# Revit family: KS, ALU-PU 80, DS 20, M10-M12, Ø 42-168,3
name_source: partatom
category: HLS-Bauteile
revit_build: Autodesk Revit 2017 (Build: 20190507_1515(x64)
units: mm (PartAtom-declared; Revit-internal decimal feet)

## family parameters
Arbeitsebenenbasiert = Ja
Beim Laden mit Abzugskörper schneiden = Nein
Bemaßung runder Anschluss = Durchmesser verwenden
Gemeinsam genutzt = Ja
Immer vertikal = Nein
Raumberechnungspunkt = Nein
Teiletyp = Normal

## types (15) — shared parameters
Anschluss = M10/M12
Baustoffklasse = B2
DS = 20 mm  [stored 0.0656168 ft]
DVS = 18 mm  [stored 0.0590551 ft]
Dichte Kern = 80 kg/m³
Dichte Mantel = 2.700 kg/m³
Dicke Mantel = 0,08 mm
Dämmkörper = ALU/PU
Dämmstärke = 20 mm  [stored 0.0656168 ft]
Fabrikat = MEFA
Firma = MEFA Befestigungs- und Montagesysteme GmbH
HGA = 22 mm  [stored 0.0721785 ft]
Kurztext1 = Kälteschelle RG80 ALU/PU
L = 100 mm
Material = Stahl
Material Mantel = Alufolie
Materialname = S235
Mengeneinheit = St
Oberflaeche = galvanisch verzinkt
Rohrschellentyp = Maxima PSM
Schalenlänge = 100 mm
Vorgabe-Ansicht = 1219 mm
Wasserdampfdiffusionswiderstand = 18750 µ
Wärmeleitfähigkeit = 0.025 W/mK
max. Temperaturbeständigkeit = 120 °C
mittl. Nenndruckfestigkeit Kern = 0,5 N/mm²
stat. Belastung Kern = 0,1 N/mm²
vpe = 1 St

## per-type parameters (varying)
- Kälteschelle ALU-PU 80, DS 20, M10/M12, Ø 42,4: A=45 mm  [stored 0.147638 ft]; AB=2 mm  [stored 0.00656168 ft]; Anschlußhöhe=46 mm; Artikelnummer=7560426; B=150 mm; Breite=151 mm; D=42 mm; D0=82 mm; DF1=31 mm  [stored 0.101706 ft]; DF2=30 mm  [stored 0.0984252 ft]; Dmax=43 mm  [stored 0.141076 ft]; Dmin=40 mm  [stored 0.131234 ft]; EAN=4250928443427; Gewicht=0.42 kg; Gewicht pro Bauteil=0.42 kg; H=110 mm; Kurztext2=42,4 mm Iso 20 x 100 mm M10/M12; MB=30 mm  [stored 0.0984252 ft]; MD=3 mm  [stored 0.00984252 ft]; R=41 mm; RM=44 mm; Rohraußendurchmesser Kupfer=42 mm; Rohraußendurchmesser Stahl=42,4 mm; S=119 mm; max. zul. Last=0.40 kN
- Kälteschelle ALU-PU 80, DS 20, M10/M12, Ø 48,3: A=45 mm  [stored 0.147638 ft]; AB=1 mm  [stored 0.00328084 ft]; Anschlußhöhe=44 mm; Artikelnummer=7560486; B=150 mm; Breite=151 mm; D=48 mm; D0=88 mm; DF1=27 mm  [stored 0.0885827 ft]; DF2=27 mm  [stored 0.0885827 ft]; Dmax=50 mm  [stored 0.164042 ft]; Dmin=47 mm  [stored 0.154199 ft]; EAN=4250928443441; Gewicht=0.42 kg; Gewicht pro Bauteil=0.42 kg; H=116 mm; Kurztext2=48,3 mm Iso 20 x 100 mm M10/M12; MB=30 mm  [stored 0.0984252 ft]; MD=3 mm  [stored 0.00984252 ft]; R=44 mm; RM=47 mm  [stored 0.154199 ft]; Rohraußendurchmesser Stahl=48,3 mm; S=123 mm; max. zul. Last=0.40 kN
- Kälteschelle ALU-PU 80, DS 20, M10/M12, Ø 54: A=45 mm  [stored 0.147638 ft]; AB=2 mm  [stored 0.00656168 ft]; Anschlußhöhe=46 mm; Artikelnummer=75605432; B=162 mm; Breite=162 mm; D=54 mm  [stored 0.177165 ft]; D0=94 mm; DF1=29 mm  [stored 0.0951444 ft]; DF2=29 mm  [stored 0.0951444 ft]; Dmax=58 mm  [stored 0.190289 ft]; Dmin=52 mm; EAN=4250928443472; Gewicht=0.46 kg; Gewicht pro Bauteil=0.46 kg; H=122 mm; Kurztext2=54 mm Iso 20 x 100 mm M10/M12; MB=30 mm  [stored 0.0984252 ft]; MD=3 mm  [stored 0.00984252 ft]; R=47 mm  [stored 0.154199 ft]; RM=50 mm  [stored 0.164042 ft]; Rohraußendurchmesser Kupfer=54 mm; S=133 mm; max. zul. Last=0.40 kN
- Kälteschelle ALU-PU 80, DS 20, M10/M12, Ø 57: A=45 mm  [stored 0.147638 ft]; AB=1 mm  [stored 0.00328084 ft]; Anschlußhöhe=45 mm; Artikelnummer=75605742; B=162 mm; Breite=162 mm; D=57 mm  [stored 0.187008 ft]; D0=97 mm; DF1=28 mm  [stored 0.0918635 ft]; DF2=28 mm  [stored 0.0918635 ft]; Dmax=60 mm  [stored 0.19685 ft]; Dmin=56 mm  [stored 0.183727 ft]; EAN=4250928443489; Gewicht=0.46 kg; Gewicht pro Bauteil=0.46 kg; H=125 mm; Kurztext2=57 mm Iso 20 x 100 mm M10/M12; MB=30 mm  [stored 0.0984252 ft]; MD=3 mm  [stored 0.00984252 ft]; R=49 mm; RM=52 mm; Rohraußendurchmesser Stahl=57 mm; S=134 mm; max. zul. Last=0.40 kN
- Kälteschelle ALU-PU 80, DS 20, M10/M12, Ø 60,3: A=45 mm  [stored 0.147638 ft]; AB=2 mm  [stored 0.00656168 ft]; Anschlußhöhe=44 mm; Artikelnummer=7560606; B=162 mm; Breite=162 mm; D=60 mm  [stored 0.19685 ft]; D0=100 mm; DF1=27 mm  [stored 0.0885827 ft]; DF2=27 mm  [stored 0.0885827 ft]; Dmax=62 mm  [stored 0.203412 ft]; Dmin=58 mm  [stored 0.190289 ft]; EAN=4250928443502; Gewicht=0.46 kg; Gewicht pro Bauteil=0.46 kg; H=128 mm; Kurztext2=60,3 mm Iso 20 x 100 mm M10/M12; MB=30 mm  [stored 0.0984252 ft]; MD=3 mm  [stored 0.00984252 ft]; R=50 mm  [stored 0.164042 ft]; RM=53 mm; Rohraußendurchmesser Stahl=60,3 mm; S=135 mm; max. zul. Last=0.40 kN
- Kälteschelle ALU-PU 80, DS 20, M10/M12, Ø 63,5: A=45 mm  [stored 0.147638 ft]; AB=2 mm  [stored 0.00656168 ft]; Anschlußhöhe=46 mm; Artikelnummer=75606442; B=172 mm; Breite=172 mm; D=64 mm; D0=104 mm; DF1=30 mm  [stored 0.0984252 ft]; DF2=30 mm  [stored 0.0984252 ft]; Dmax=66 mm  [stored 0.216535 ft]; Dmin=62 mm  [stored 0.203412 ft]; EAN=4250928443526; Gewicht=0.49 kg; Gewicht pro Bauteil=0.49 kg; H=132 mm; Kurztext2=63,5 mm Iso 20 x 100 mm M10/M12; MB=30 mm  [stored 0.0984252 ft]; MD=3 mm  [stored 0.00984252 ft]; R=52 mm; RM=55 mm  [stored 0.180446 ft]; Rohraußendurchmesser Stahl=63,5 mm; S=142 mm; max. zul. Last=0.50 kN
- Kälteschelle ALU-PU 80, DS 20, M10/M12, Ø 70: A=45 mm  [stored 0.147638 ft]; AB=2 mm  [stored 0.00656168 ft]; Anschlußhöhe=44 mm; Artikelnummer=75607042; B=172 mm; Breite=172 mm; D=70 mm; D0=110 mm; DF1=27 mm  [stored 0.0885827 ft]; DF2=27 mm  [stored 0.0885827 ft]; Dmax=72 mm; Dmin=68 mm; EAN=4250928443540; Gewicht=0.48 kg; Gewicht pro Bauteil=0.48 kg; H=138 mm; Kurztext2=70 mm Iso 20 x 100 mm M10/M12; MB=30 mm  [stored 0.0984252 ft]; MD=3 mm  [stored 0.00984252 ft]; R=55 mm  [stored 0.180446 ft]; RM=58 mm  [stored 0.190289 ft]; Rohraußendurchmesser Stahl=70 mm; S=145 mm; max. zul. Last=0.50 kN
- Kälteschelle ALU-PU 80, DS 20, M10/M12, Ø 76,1: A=45 mm  [stored 0.147638 ft]; AB=2 mm  [stored 0.00656168 ft]; Anschlußhöhe=47 mm; Artikelnummer=7560766; B=184 mm; Breite=184 mm; D=76 mm; D0=116 mm; DF1=29 mm  [stored 0.0951444 ft]; DF2=29 mm  [stored 0.0951444 ft]; Dmax=80 mm; Dmin=74 mm; EAN=4250928443571; Gewicht=0.53 kg; Gewicht pro Bauteil=0.53 kg; H=144 mm; Kurztext2=76,1 mm Iso 20 x 100 mm M10/M12; MB=30 mm  [stored 0.0984252 ft]; MD=3 mm  [stored 0.00984252 ft]; R=58 mm  [stored 0.190289 ft]; RM=61 mm; Rohraußendurchmesser Stahl=76,1 mm; S=155 mm; max. zul. Last=0.50 kN
- Kälteschelle ALU-PU 80, DS 20, M10/M12, Ø 88,9: A=46 mm  [stored 0.150919 ft]; AB=3 mm  [stored 0.00984252 ft]; Anschlußhöhe=47 mm; Artikelnummer=7560896; B=210 mm; Breite=209 mm; D=89 mm; D0=129 mm; DF1=35 mm  [stored 0.114829 ft]; DF2=35 mm  [stored 0.114829 ft]; Dmax=92 mm; Dmin=86 mm; EAN=4250928443588; Gewicht=0.77 kg; Gewicht pro Bauteil=0.77 kg; H=159 mm; Kurztext2=88,9 mm Iso 20 x 100 mm M10/M12; MB=35 mm  [stored 0.114829 ft]; MD=4 mm  [stored 0.0131234 ft]; R=64 mm; RM=68 mm; Rohraußendurchmesser Stahl=88,9 mm; S=175 mm; max. zul. Last=0.70 kN
- Kälteschelle ALU-PU 80, DS 20, M10/M12, Ø108: A=46 mm  [stored 0.150919 ft]; AB=2 mm  [stored 0.00656168 ft]; Anschlußhöhe=46 mm; Artikelnummer=75610844; B=227 mm; Breite=226 mm; D=108 mm; D0=148 mm; DF1=34 mm; DF2=35 mm  [stored 0.114829 ft]; Dmax=110 mm; Dmin=106 mm; EAN=4250928443601; Gewicht=0.84 kg; Gewicht pro Bauteil=0.84 kg; H=178 mm; Kurztext2=108 mm Iso 20 x 100 mm M10/M12; MB=35 mm  [stored 0.114829 ft]; MD=4 mm  [stored 0.0131234 ft]; R=74 mm; RM=78 mm; Rohraußendurchmesser Stahl=108 mm; S=193 mm; max. zul. Last=0.80 kN
- Kälteschelle ALU-PU 80, DS 20, M10/M12, Ø114,3: A=46 mm  [stored 0.150919 ft]; AB=2 mm  [stored 0.00656168 ft]; Anschlußhöhe=47 mm; Artikelnummer=75611444; B=235 mm; Breite=234 mm; D=114 mm; D0=154 mm; DF1=35 mm  [stored 0.114829 ft]; DF2=36 mm  [stored 0.11811 ft]; Dmax=116 mm; Dmin=112 mm; EAN=4250928443625; Gewicht=0.87 kg; Gewicht pro Bauteil=0.87 kg; H=184 mm; Kurztext2=114,3 mm Iso 20 x 100 mm M10/M12; MB=35 mm  [stored 0.114829 ft]; MD=4 mm  [stored 0.0131234 ft]; R=77 mm; RM=81 mm; Rohraußendurchmesser Stahl=114,3 mm; S=200 mm; max. zul. Last=0.80 kN
- Kälteschelle ALU-PU 80, DS 20, M10/M12, Ø133: A=46 mm  [stored 0.150919 ft]; AB=1 mm  [stored 0.00328084 ft]; Anschlußhöhe=47 mm; Artikelnummer=75613344; B=253 mm; Breite=252 mm; D=133 mm; D0=173 mm; DF1=35 mm  [stored 0.114829 ft]; DF2=35 mm  [stored 0.114829 ft]; Dmax=135 mm; Dmin=132 mm; EAN=4250928443649; Gewicht=0.95 kg; Gewicht pro Bauteil=0.95 kg; H=203 mm; Kurztext2=133 mm Iso 20 x 100 mm M10/M12; MB=35 mm  [stored 0.114829 ft]; MD=4 mm  [stored 0.0131234 ft]; R=87 mm; RM=91 mm; Rohraußendurchmesser Stahl=133 mm; S=218 mm; max. zul. Last=0.90 kN
- Kälteschelle ALU-PU 80, DS 20, M10/M12, Ø139,7: A=46 mm  [stored 0.150919 ft]; AB=2 mm  [stored 0.00656168 ft]; Anschlußhöhe=45 mm; Artikelnummer=75614044; B=253 mm; Breite=252 mm; D=140 mm; D0=180 mm; DF1=32 mm  [stored 0.104987 ft]; DF2=33 mm  [stored 0.108268 ft]; Dmax=140 mm; Dmin=138 mm; EAN=4250928443700; Gewicht=0.94 kg; Gewicht pro Bauteil=0.94 kg; H=210 mm; Kurztext2=139,7 mm Iso 20 x 100 mm M10/M12; MB=35 mm  [stored 0.114829 ft]; MD=4 mm  [stored 0.0131234 ft]; R=90 mm; RM=94 mm; Rohraußendurchmesser Stahl=139,7 mm; S=221 mm; max. zul. Last=0.90 kN
- Kälteschelle ALU-PU 80, DS 20, M10/M12, Ø159: A=46 mm  [stored 0.150919 ft]; AB=1 mm  [stored 0.00328084 ft]; Anschlußhöhe=47 mm; Artikelnummer=75615944; B=277 mm; Breite=278 mm; D=159 mm; D0=199 mm; DF1=32 mm  [stored 0.104987 ft]; DF2=33 mm  [stored 0.108268 ft]; Dmax=164 mm; Dmin=158 mm; EAN=4250928443748; Gewicht=1.06 kg; Gewicht pro Bauteil=1.06 kg; H=229 mm; Kurztext2=159 mm Iso 20 x 100 mm M10/M12; MB=35 mm  [stored 0.114829 ft]; MD=4 mm  [stored 0.0131234 ft]; R=100 mm; RM=104 mm; Rohraußendurchmesser Stahl=159 mm; S=245 mm; max. zul. Last=1.00 kN
- Kälteschelle ALU-PU 80, DS 20, M10/M12, Ø168,3: A=46 mm  [stored 0.150919 ft]; AB=1 mm  [stored 0.00328084 ft]; Anschlußhöhe=46 mm; Artikelnummer=75616844; B=288 mm; Breite=287 mm; D=168 mm; D0=208 mm; DF1=34 mm; DF2=34 mm; Dmax=172 mm; Dmin=167 mm; EAN=4250928443786; Gewicht=1.09 kg; Gewicht pro Bauteil=1.09 kg; H=238 mm; Kurztext2=168,3 mm Iso 20 x 100 mm M10/M12; MB=35 mm  [stored 0.114829 ft]; MD=4 mm  [stored 0.0131234 ft]; R=104 mm; RM=108 mm; Rohraußendurchmesser Stahl=168,3 mm; S=254 mm; max. zul. Last=1.10 kN

note: [stored X ft] marks values corroborated as IEEE doubles in the binary element streams (Revit-internal decimal feet)

## geometry (parser evidence)
native form markers: Sweep x6
no freeform markers — native parametric forms only
